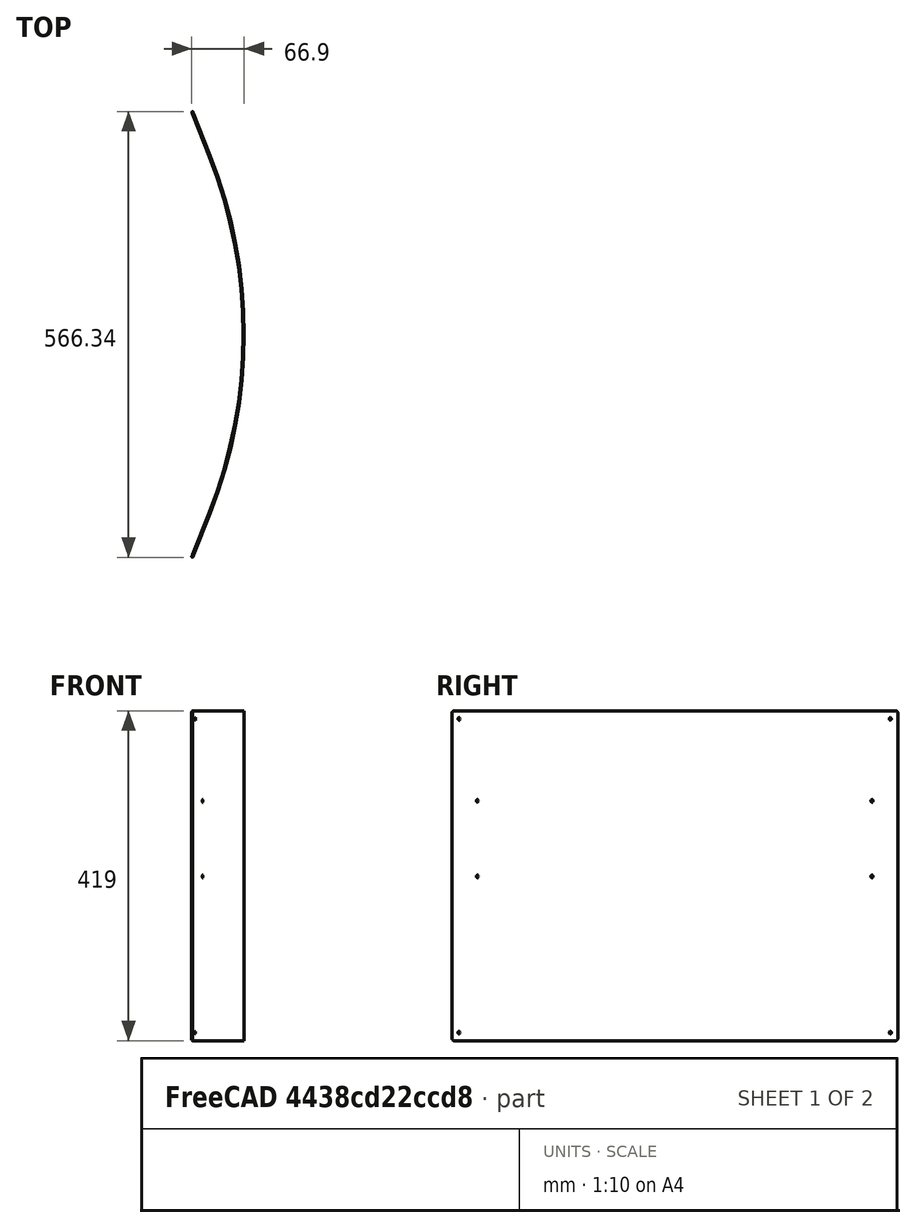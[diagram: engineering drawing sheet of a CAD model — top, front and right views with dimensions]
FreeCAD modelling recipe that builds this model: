
FCSTD DOCUMENT  (FreeCAD 1.1R38827 (Git))
Label: composit_stand3_tech_sector_plexiglass_main
License: All rights reserved
LicenseURL: http://en.wikipedia.org/wiki/All_rights_reserved
objects: Part::FeaturePython×2, Sketcher::SketchObject×1, Part::Feature×1
note: 5 computed .brp shape members not serialized (recipe doc carries the construction recipe); baked Part::Feature solids carry a one-line shape summary decoded from their .brp
EXTERNAL_REF file=composit_stand3_tech_sector_pillar_main.FCStd obj=Sketch

FEATURE [Sketcher::SketchObject] Sketch  label="main_sketch"
  ArcFitTolerance = 0
  FullyConstrained = true
  MakeInternals = false
  expr: .Constraints.angle = 60 deg + <<composit_stand3_tech_sector_pillar_main>>#<<Sketch>>.Constraints.angle
  expr: Constraints[5] = <<composit_stand3_tech_sector_pillar_main>>#<<Sketch>>.Constraints.front
  sketch-geometry (3):
    g0: LineSegment StartX=202.67 StartY=226.752 StartZ=0 EndX=180.364 EndY=283.047 EndZ=0
    g1: ArcOfCircle CenterX=-357 CenterY=5 CenterZ=0 NormalX=0 NormalY=0 NormalZ=1 AngleXU=0 Radius=602 StartAngle=0 EndAngle=0.377243
    g2: LineSegment StartX=245 StartY=5 StartZ=0 EndX=245 EndY=0 EndZ=0
  constraints (9):
    c: Angle(g0) = 1.94804  'angle'
    c: Tangent(g0,g1) = -1.5708
    c: Vertical(g2)
    c: Tangent(g2,g1) = 1.5708
    c: DistanceY(g2,g2) = 5
    c: Distance(g0) = 60.5533
    c: PointOnObject(g2,g-1)
    c: Radius(g1) = 602  'r'
    c: DistanceX(g2) = 245  'offset'
FEATURE [Part::Feature] Body160  label="tech_sector_plexiglass_material_0.30ansi001"
  Placement = pos=(0,0,0) rot=(0,0,-1;0.523599rad)
  shape: bbox 73.31 x 566.4 x 419 mm, 26 faces (baked)
FEATURE [Part::FeaturePython] Placment  label="edge_placement"  # WARN: FeaturePython — macro-defined, semantics opaque (R4)
  AttacherType = Attacher::AttachEngine3D
  AttachmentOffset = pos=(0,0,0) rot=(-0.57735,0.57735,0.57735;2.0944rad)
  AttachmentSupport = -> [Sketch]
  ExposePlacement = true
  MapMode = 7
  MarkerShape = 1
  MarkerSize = 50
  NumElements = 1
  Placement = pos=(180.364,283.047,0) rot=(0,0,1;1.94804rad)
  Type = lattice2AttachablePlacement.AttachablePlacement
  isLattice = 1
FEATURE [Part::FeaturePython] Placment001  label="fix_corner_placement"  # WARN: FeaturePython — macro-defined, semantics opaque (R4)
  AttacherType = Attacher::AttachEngine3D
  ExposePlacement = true
  MarkerShape = 1
  MarkerSize = 200
  NumElements = 1
  Placement = pos=(245,0,3) rot=(0,0,1;1.5708rad)
  Type = lattice2AttachablePlacement.AttachablePlacement
  isLattice = 1
  expr: .Placement.Base.x = <<main_sketch>>.Constraints.offset
